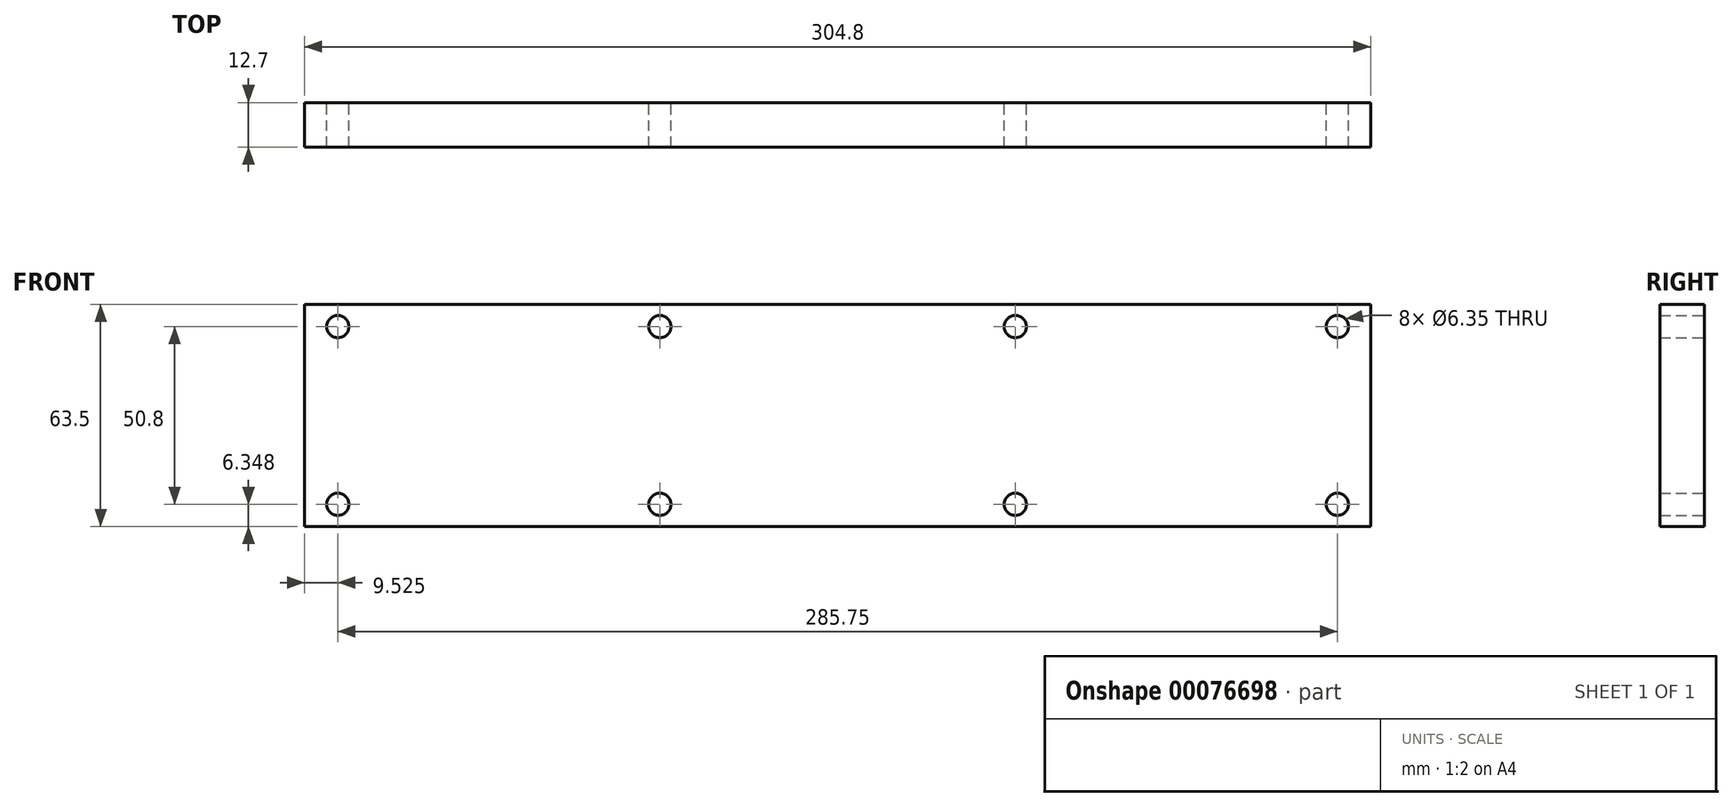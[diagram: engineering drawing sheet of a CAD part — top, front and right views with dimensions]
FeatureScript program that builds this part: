
annotation { "Feature Type Name" : "Feature", "Feature Type Description" : "" }
export const myFeature = defineFeature(function(context is Context, id is Id, definition is map)
    precondition{}
    {
        {
            var Q0;
            Q0=qCreatedBy(makeId("Front.planeOp"),FACE);
            var sketch = newSketch(context, id + "F0", { "sketchPlane" : qUnion([Q0])});
            skLineSegment(sketch, "E0.bottom", {"start": v(-155.17, 43.3) * mm, "end": v(149.63, 43.3) * mm});
            skLineSegment(sketch, "E0.top", {"start": v(-155.17, -20.2) * mm, "end": v(149.63, -20.2) * mm});
            skLineSegment(sketch, "E0.left", {"start": v(-155.17, 43.3) * mm, "end": v(-155.17, -20.2) * mm});
            skLineSegment(sketch, "E0.right", {"start": v(149.63, 43.3) * mm, "end": v(149.63, -20.2) * mm});
            skCircle(sketch, "E1", {"center": v(-145.64, 36.95) * mm, "radius": 3.18 * mm});
            skCircle(sketch, "E2", {"center": v(-53.57, 36.95) * mm, "radius": 3.18 * mm});
            skCircle(sketch, "E3", {"center": v(48.03, 36.95) * mm, "radius": 3.18 * mm});
            skCircle(sketch, "E4", {"center": v(140.1, 36.95) * mm, "radius": 3.18 * mm});
            skCircle(sketch, "E5", {"center": v(140.1, -13.85) * mm, "radius": 3.18 * mm});
            skCircle(sketch, "E6", {"center": v(48.03, -13.85) * mm, "radius": 3.18 * mm});
            skCircle(sketch, "E7", {"center": v(-53.57, -13.85) * mm, "radius": 3.18 * mm});
            skCircle(sketch, "E8", {"center": v(-145.64, -13.85) * mm, "radius": 3.18 * mm});
            skLineSegment(sketch, "E9.0", {"start": v(-155.17, 30.6) * mm, "end": v(149.63, 30.6) * mm, "construction": true});
            skLineSegment(sketch, "E10.0", {"start": v(116.61, 43.3) * mm, "end": v(116.61, -20.2) * mm, "construction": true});
            skLineSegment(sketch, "E11.0", {"start": v(-155.17, 5.2) * mm, "end": v(149.63, 5.2) * mm, "construction": true});
            skSolve(sketch);
        }
        {
            var Q0;
            Q0=makeQuery(id+"F0.imprint","IMPRINT",FACE,{"disambiguationData":[TD([[makeQuery(id+"F0.imprint","IMPRINT",EDGE,{"derivedFrom":sQuery(id+"F0.wireOp",EDGE,"E0.bottom")}),-1.0]])]});
            extrude(context, id + "F1", {"entities" : qUnion([Q0]), "depth" : 12.7 * mm});
        }
    });
